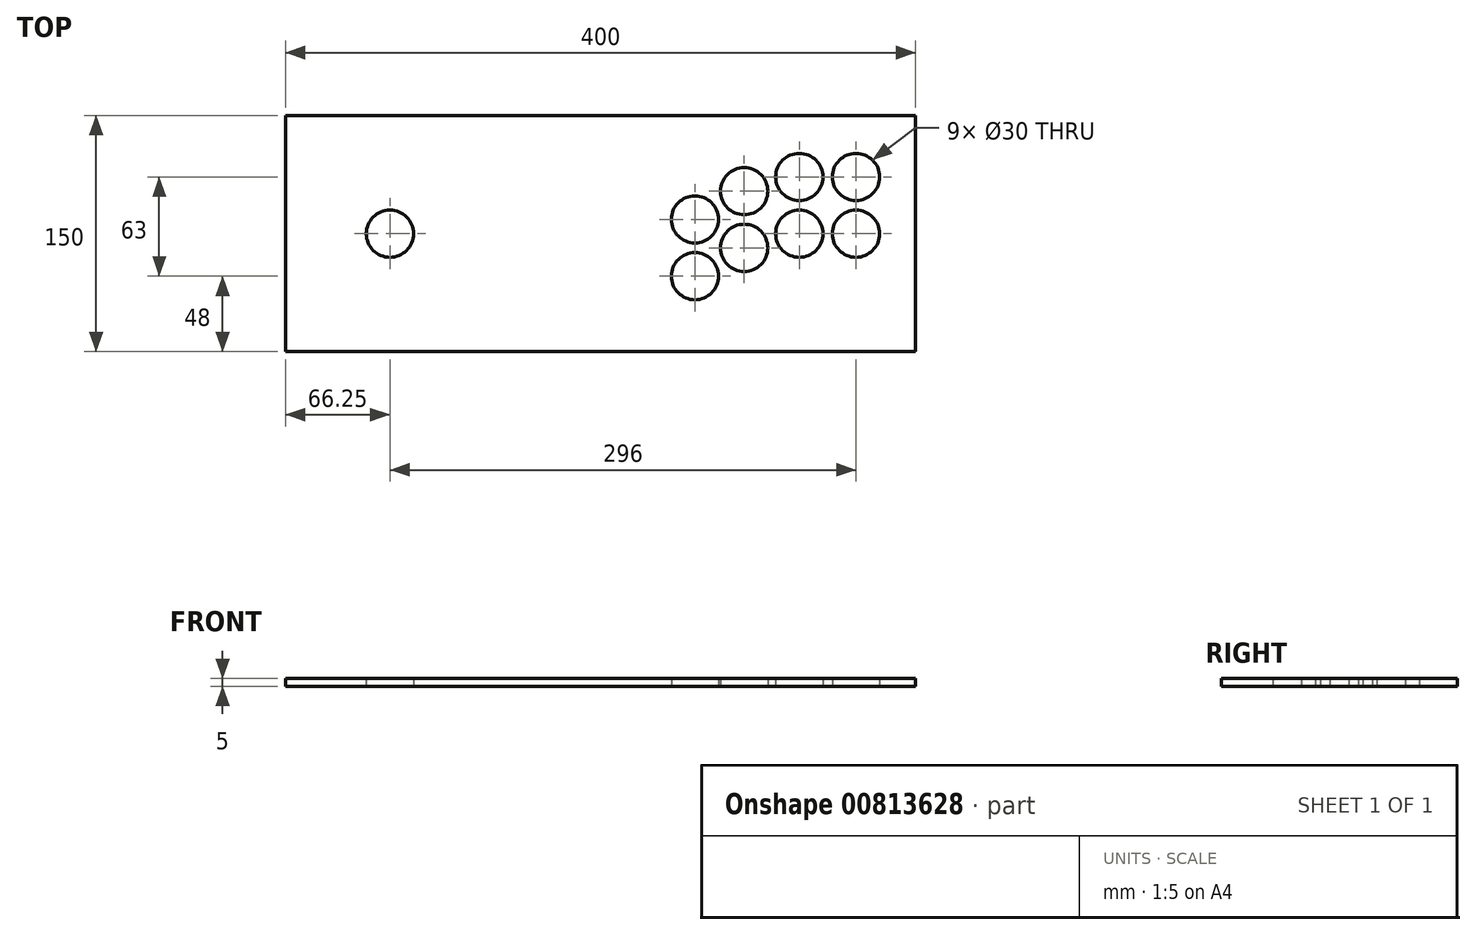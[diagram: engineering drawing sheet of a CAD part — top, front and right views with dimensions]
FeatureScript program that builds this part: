
annotation { "Feature Type Name" : "Feature", "Feature Type Description" : "" }
export const myFeature = defineFeature(function(context is Context, id is Id, definition is map)
    precondition{}
    {
        {
            var Q0;
            Q0=qCreatedBy(makeId("Top.planeOp"),FACE);
            var sketch = newSketch(context, id + "F0", { "sketchPlane" : qUnion([Q0])});
            skLineSegment(sketch, "E0.bottom", {"start": v(200, -75) * mm, "end": v(-200, -75) * mm});
            skLineSegment(sketch, "E0.top", {"start": v(200, 75) * mm, "end": v(-200, 75) * mm});
            skLineSegment(sketch, "E0.left", {"start": v(200, -75) * mm, "end": v(200, 75) * mm});
            skLineSegment(sketch, "E0.right", {"start": v(-200, -75) * mm, "end": v(-200, 75) * mm});
            skPoint(sketch, "E0.middle", {"position": v(0, 0) * mm});
            skCircle(sketch, "E1", {"center": v(-133.75, 0) * mm, "radius": 15 * mm});
            skCircle(sketch, "E2", {"center": v(126.25, 0) * mm, "radius": 15 * mm});
            skCircle(sketch, "E3", {"center": v(126.25, 36) * mm, "radius": 15 * mm});
            skCircle(sketch, "E4", {"center": v(162.25, 36) * mm, "radius": 15 * mm});
            skCircle(sketch, "E5", {"center": v(162.25, 0) * mm, "radius": 15 * mm});
            skCircle(sketch, "E6", {"center": v(91.25, -9) * mm, "radius": 15 * mm});
            skCircle(sketch, "E7", {"center": v(91.25, 27) * mm, "radius": 15 * mm});
            skCircle(sketch, "E8", {"center": v(60, -27) * mm, "radius": 15 * mm});
            skCircle(sketch, "E9", {"center": v(60, 9) * mm, "radius": 15 * mm});
            skSolve(sketch);
        }
        {
            var Q0;
            Q0 = qSketchRegion(id + "F0", true);
            extrude(context, id + "F1", {"entities" : qUnion([Q0]), "depth" : 5 * mm, "offsetDistance" : 25 * mm});
        }
    });
